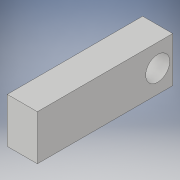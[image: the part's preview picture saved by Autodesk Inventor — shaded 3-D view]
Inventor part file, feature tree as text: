
AUTODESK INVENTOR PART (.ipt)
format: ipt  version: 2019 (Build 230136000, 136)  size: 98,304 bytes
history: native  units: in
note: dims shown in document units (in); Inventor stores cm internally (conversion verified against a paired STEP export)
features: sketch x2, extrude x1, hole x1, projected_geometry x1
ambient origin geometry x8: Origin, YZ Plane, XZ Plane, XY Plane, X Axis, Y Axis, Z Axis, Center Point
bodies: Solid1 (feature_tree)
feature tree (5):
  extrude  "Extrusion1"  Depth=0.5in
  hole  "Hole1"  [1 undecoded]
  sketch  "Sketch1"  dims[d0=2.25in d1=0.5in]
  sketch  "Sketch2"  dims[d2=0.75in d3=0.0in d4=2.0in d5=0.4in d6=0.75in d7=0.375in d8=0.25in d9=0.5635in d10=0.4in d11=0.0in]
  projected_geometry  "Projected Loop1"
note: 1 required parameter value undecoded (feature->parameter linkage not recoverable at this tier; creation-order binding heuristic only, values carry confidence <= 0.55)
